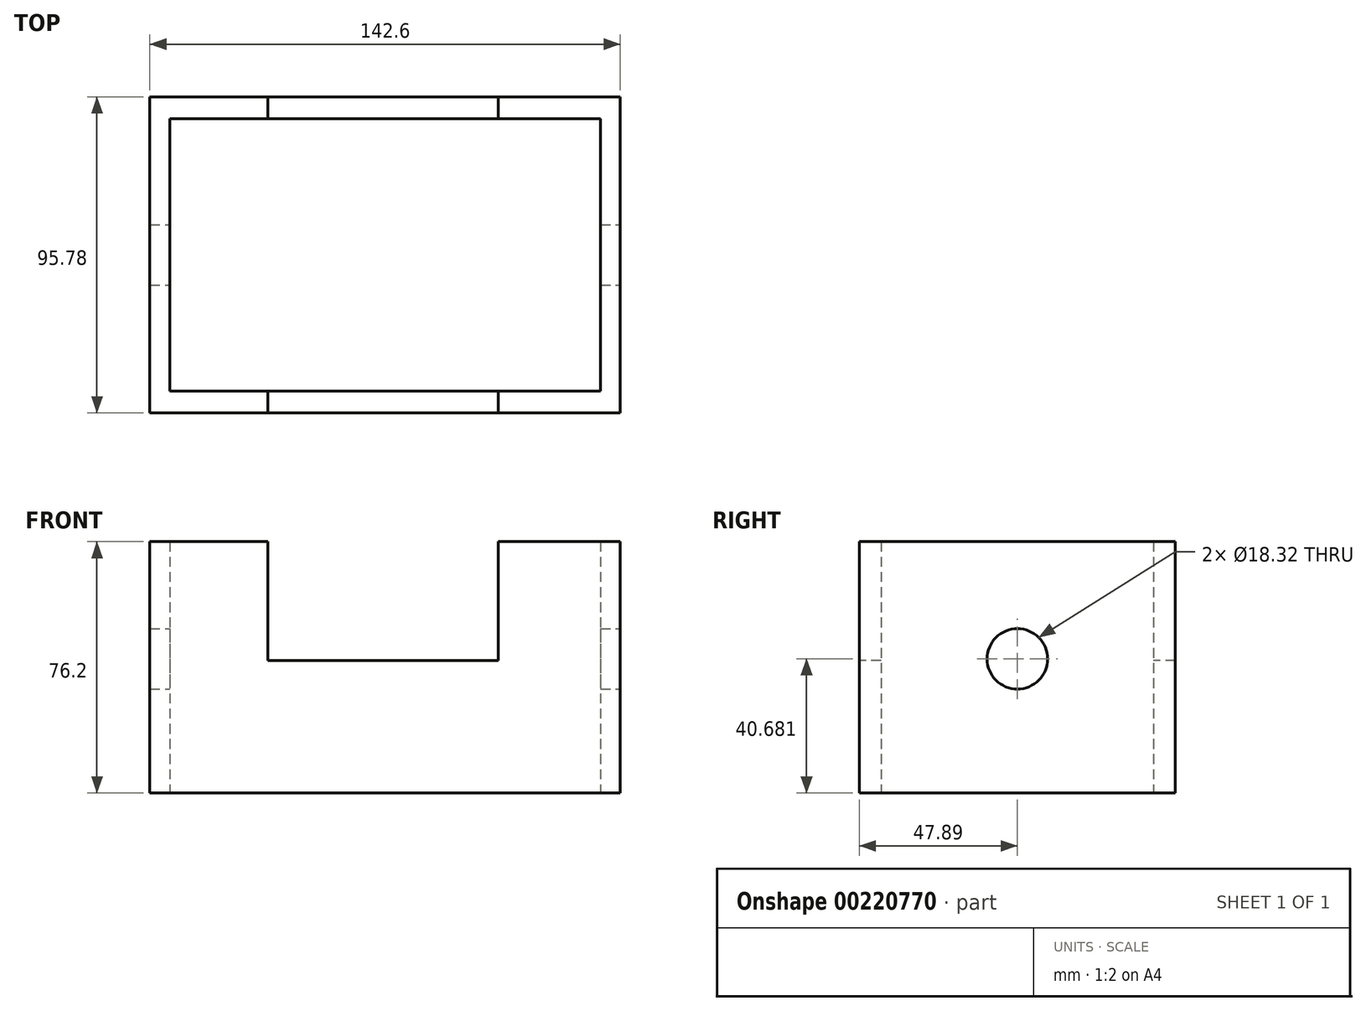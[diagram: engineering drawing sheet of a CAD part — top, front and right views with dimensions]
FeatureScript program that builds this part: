
annotation { "Feature Type Name" : "Feature", "Feature Type Description" : "" }
export const myFeature = defineFeature(function(context is Context, id is Id, definition is map)
    precondition{}
    {
        {
            var Q0;
            Q0=qCreatedBy(makeId("Top.planeOp"),FACE);
            var sketch = newSketch(context, id + "F0", { "sketchPlane" : qUnion([Q0])});
            skLineSegment(sketch, "E0.bottom", {"start": v(71.3, -47.89) * mm, "end": v(-71.3, -47.89) * mm});
            skLineSegment(sketch, "E0.top", {"start": v(71.3, 47.89) * mm, "end": v(-71.3, 47.89) * mm});
            skLineSegment(sketch, "E0.left", {"start": v(71.3, -47.89) * mm, "end": v(71.3, 47.89) * mm});
            skLineSegment(sketch, "E0.right", {"start": v(-71.3, -47.89) * mm, "end": v(-71.3, 47.89) * mm});
            skPoint(sketch, "E0.middle", {"position": v(0, 0) * mm});
            skLineSegment(sketch, "E1.bottom", {"start": v(65.3, -41.28) * mm, "end": v(-65.3, -41.28) * mm});
            skLineSegment(sketch, "E1.top", {"start": v(65.3, 41.28) * mm, "end": v(-65.3, 41.28) * mm});
            skLineSegment(sketch, "E1.left", {"start": v(65.3, -41.28) * mm, "end": v(65.3, 41.28) * mm});
            skLineSegment(sketch, "E1.right", {"start": v(-65.3, -41.28) * mm, "end": v(-65.3, 41.28) * mm});
            skSolve(sketch);
        }
        {
            var Q0;
            Q0 = qSketchRegion(id + "F0", true);
            extrude(context, id + "F1", {"entities" : qUnion([Q0]), "depth" : 76.2 * mm});
        }
        {
            var Q0;
            Q0=makeQuery(id+"F1.opExtrude","SWEPT_FACE",FACE,{"disambiguationData":[OSD([sQuery(id+"F0.wireOp",EDGE,"E0.bottom")])]});
            var sketch = newSketch(context, id + "F2", { "sketchPlane" : qUnion([Q0])});
            skLineSegment(sketch, "E2.bottom", {"start": v(-35.58, 76.2) * mm, "end": v(34.3, 76.2) * mm});
            skLineSegment(sketch, "E2.top", {"start": v(-35.58, 40.18) * mm, "end": v(34.3, 40.18) * mm});
            skLineSegment(sketch, "E2.left", {"start": v(-35.58, 76.2) * mm, "end": v(-35.58, 40.18) * mm});
            skLineSegment(sketch, "E2.right", {"start": v(34.3, 76.2) * mm, "end": v(34.3, 40.18) * mm});
            skSolve(sketch);
        }
        {
            var Q0;
            Q0=makeQuery(id+"F2.imprint","IMPRINT",FACE,{"disambiguationData":[TD([[makeQuery(id+"F2.imprint","IMPRINT",EDGE,{"derivedFrom":sQuery(id+"F2.wireOp",EDGE,"E2.bottom")}),1.0]])]});
            extrude(context, id + "F3", {"entities" : qUnion([Q0]), "operationType" : NewBodyOperationType.REMOVE, "oppositeDirection" : true, "depth" : 127 * mm});
        }
        {
            var Q0;
            Q0=makeQuery(id+"F1.opExtrude","SWEPT_FACE",FACE,{"disambiguationData":[OSD([sQuery(id+"F0.wireOp",EDGE,"E0.left")])]});
            var sketch = newSketch(context, id + "F4", { "sketchPlane" : qUnion([Q0])});
            skCircle(sketch, "E3", {"center": v(0, 40.68) * mm, "radius": 9.16 * mm});
            skSolve(sketch);
        }
        {
            var Q0;
            Q0=makeQuery(id+"F4.imprint","IMPRINT",FACE,{"disambiguationData":[TD([[makeQuery(id+"F4.imprint","IMPRINT",EDGE,{"derivedFrom":sQuery(id+"F4.wireOp",EDGE,"E3")}),1.0]])]});
            extrude(context, id + "F5", {"entities" : qUnion([Q0]), "operationType" : NewBodyOperationType.REMOVE, "oppositeDirection" : true, "depth" : 177.8 * mm});
        }
    });
